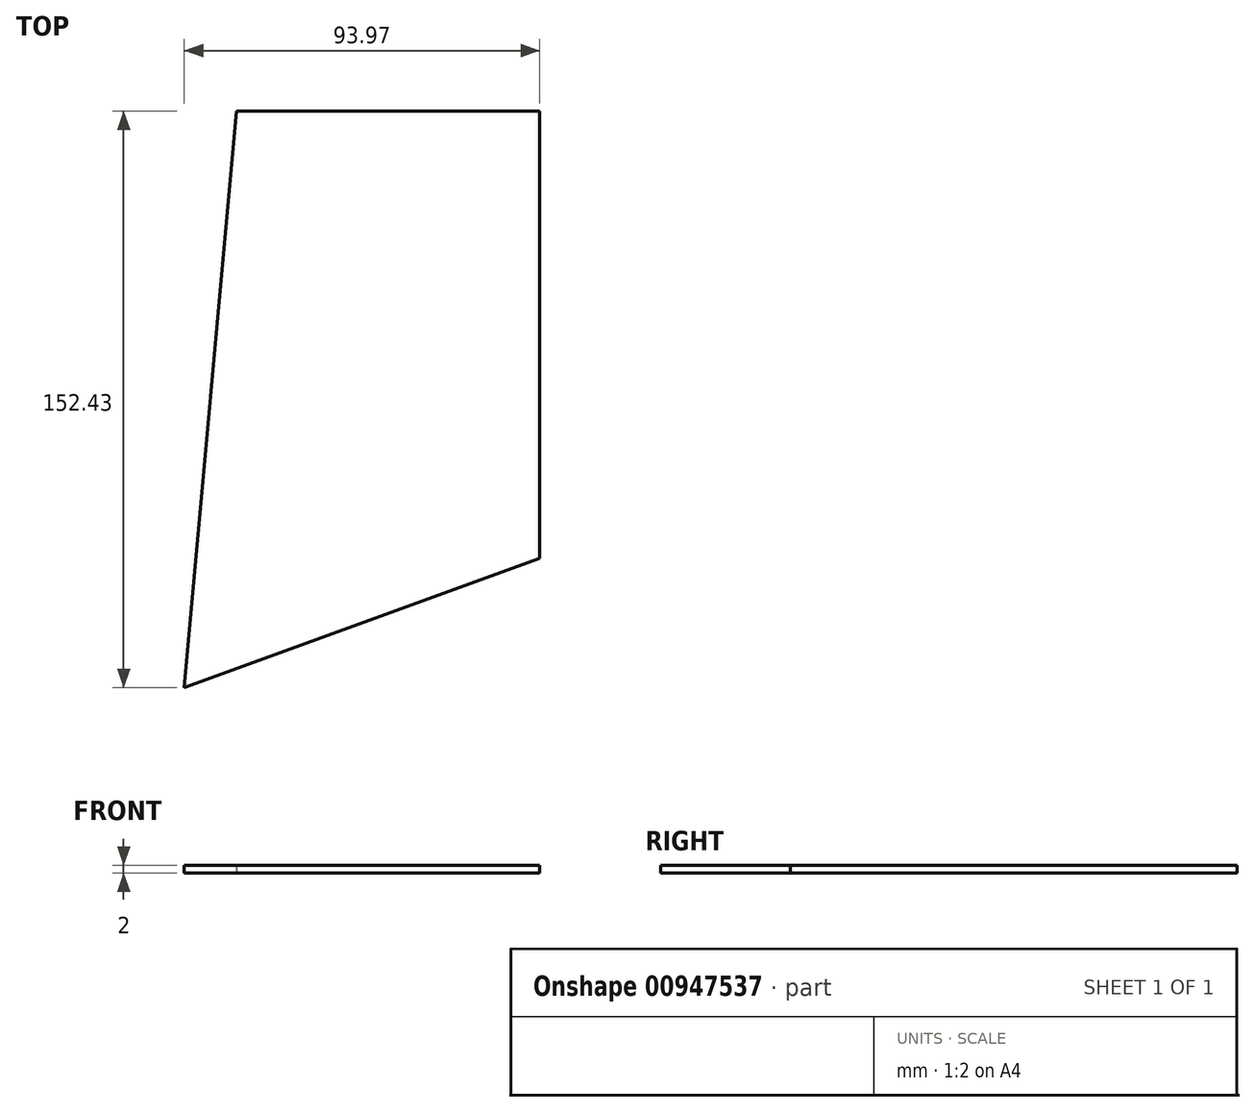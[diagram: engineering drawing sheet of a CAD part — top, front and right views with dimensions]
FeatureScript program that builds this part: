
annotation { "Feature Type Name" : "Feature", "Feature Type Description" : "" }
export const myFeature = defineFeature(function(context is Context, id is Id, definition is map)
    precondition{}
    {
        {
            var Q0;
            Q0=qCreatedBy(makeId("Top.planeOp"),FACE);
            var sketch = newSketch(context, id + "F0", { "sketchPlane" : qUnion([Q0])});
            skLineSegment(sketch, "E0", {"start": v(-117.5, -57.45) * mm, "end": v(-103.77, 94.98) * mm});
            skLineSegment(sketch, "E1", {"start": v(-117.5, -57.45) * mm, "end": v(-23.53, -23.25) * mm});
            skLineSegment(sketch, "E2", {"start": v(-23.53, -23.25) * mm, "end": v(-23.53, 94.98) * mm});
            skLineSegment(sketch, "E3", {"start": v(-23.53, 94.98) * mm, "end": v(-103.77, 94.98) * mm});
            skSolve(sketch);
        }
        {
            var Q0;
            Q0=makeQuery(id+"F0.imprint","IMPRINT",FACE,{"disambiguationData":[TD([[makeQuery(id+"F0.imprint","IMPRINT",EDGE,{"derivedFrom":sQuery(id+"F0.wireOp",EDGE,"E0")}),-1.0]])]});
            extrude(context, id + "F1", {"entities" : qUnion([Q0]), "depth" : 2 * mm, "offsetDistance" : 25 * mm});
        }
    });
